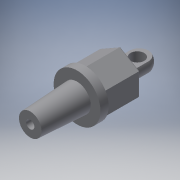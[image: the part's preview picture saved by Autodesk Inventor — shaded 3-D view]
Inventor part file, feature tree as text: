
AUTODESK INVENTOR PART (.ipt)
format: ipt  version: 2016 (Build 200138000, 138)  size: 190,464 bytes
history: native  units: mm
features: extrude x7, sketch x7, fillet x4, draft x1, plane x1
ambient origin geometry x8: Origin, YZ Plane, XZ Plane, XY Plane, X Axis, Y Axis, Z Axis, Center Point
bodies: Solid1 (feature_tree)
feature tree (20):
  extrude  "Extrusion1"  Depth=17.0mm TaperAngle=0.0deg
  extrude  "Extrusion2"  Depth=12.8mm TaperAngle=0.0deg
  fillet  "Fillet1"  Radius=0.5mm
  extrude  "Extrusion3"  Depth=0.8mm TaperAngle=0.0deg
  extrude  "Extrusion4"  Depth=9.8mm TaperAngle=0.0deg
  extrude  "Extrusion5"  Depth=5.0mm
  fillet  "Fillet3"  Radius=3.406614mm
  extrude  "Extrusion6"  Depth=9.8mm TaperAngle=0.0deg
  draft  "FaceDraft1"
  extrude  "Extrusion7"  Depth=10.0mm
  fillet  "Fillet4"  Radius=17.0mm
  plane  "Work Plane1"
  fillet  "Fillet5"  Radius=0.523599mm
  sketch  "Sketch1"  dims[d0=17.0mm d1=3.0mm d2=0.0mm]
  sketch  "Sketch2"  dims[d3=14.0mm d4=12.8mm d5=0.0mm d6=0.5mm]
  sketch  "Sketch3"  dims[d7=7.7mm d8=0.8mm d9=0.0mm]
  sketch  "Sketch4"  dims[d11=3.6mm d12=9.8mm d13=0.0mm]
  sketch  "Sketch5"  dims[d15=5.0mm d16=3.4mm d17=3.406614mm]
  sketch  "Sketch6"  dims[d18=4.5mm d19=9.8mm d20=0.0mm]
  sketch  "Sketch8"  dims[d21=3.85mm d22=10.0mm d23=17.0mm d24=0.0mm d25=0.523599mm d26=3.0mm d27=15.0mm d28=0.0mm d29=0.3mm d30=0.6mm]
